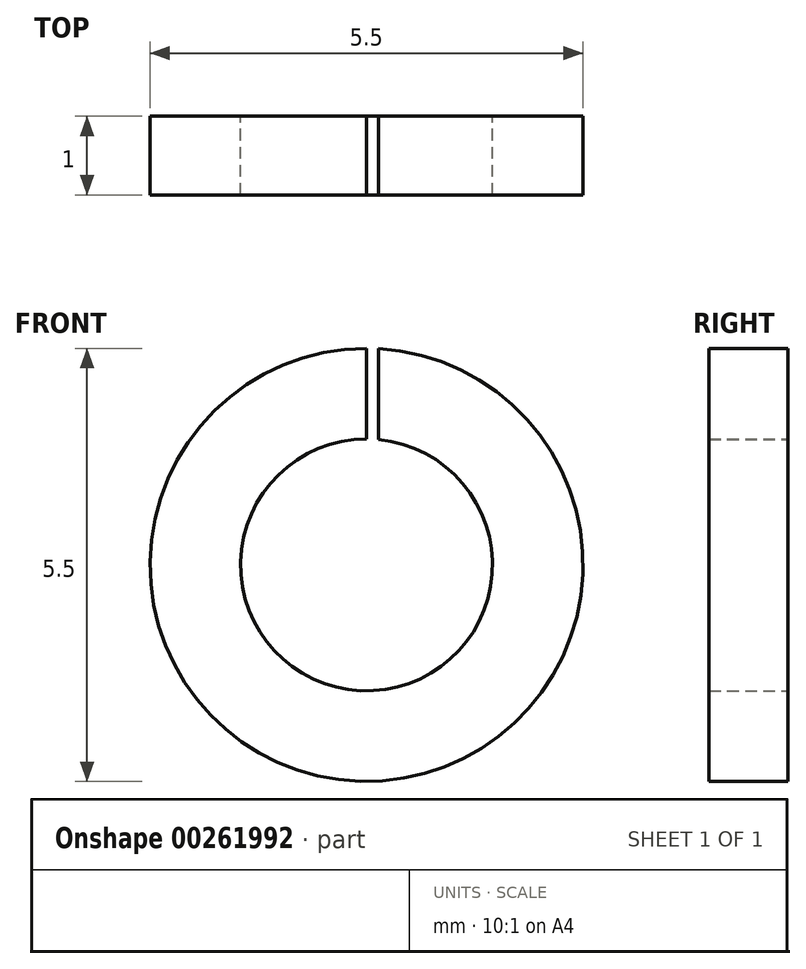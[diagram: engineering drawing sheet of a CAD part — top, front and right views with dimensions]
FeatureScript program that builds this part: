
annotation { "Feature Type Name" : "Feature", "Feature Type Description" : "" }
export const myFeature = defineFeature(function(context is Context, id is Id, definition is map)
    precondition{}
    {
        {
            assignVariable(context, id + "F0", {"name" : "Hieght", "anyValue" : 1});
        }
        {
            var Q0;
            Q0=qCreatedBy(makeId("Front.planeOp"),FACE);
            var sketch = newSketch(context, id + "F1", { "sketchPlane" : qUnion([Q0])});
            skCircle(sketch, "E0", {"center": v(0, 0) * mm, "radius": 1.6 * mm});
            skCircle(sketch, "E1", {"center": v(0, 0) * mm, "radius": 2.75 * mm});
            skSolve(sketch);
        }
        {
            var Q0;
            Q0=makeQuery(id+"F1.imprint","IMPRINT",FACE,{"disambiguationData":[TD([[makeQuery(id+"F1.imprint","IMPRINT",EDGE,{"derivedFrom":sQuery(id+"F1.wireOp",EDGE,"E0")}),-1.0]])]});
            extrude(context, id + "F2", {"entities" : qUnion([Q0]), "depth" : getVariable(context, 'Hieght') * mm});
        }
        {
            var Q0;
            Q0=qCreatedBy(makeId("Front.planeOp"),FACE);
            var sketch = newSketch(context, id + "F3", { "sketchPlane" : qUnion([Q0])});
            skLineSegment(sketch, "E2.bottom", {"start": v(0, 2.75) * mm, "end": v(0.15, 2.75) * mm});
            skLineSegment(sketch, "E2.top", {"start": v(0, 0) * mm, "end": v(0.15, 0) * mm});
            skLineSegment(sketch, "E2.left", {"start": v(0, 2.75) * mm, "end": v(0, 0) * mm});
            skLineSegment(sketch, "E2.right", {"start": v(0.15, 2.75) * mm, "end": v(0.15, 0) * mm});
            skSolve(sketch);
        }
        {
            var Q0;
            Q0=makeQuery(id+"F3.imprint","IMPRINT",FACE,{"disambiguationData":[TD([[makeQuery(id+"F3.imprint","IMPRINT",EDGE,{"derivedFrom":sQuery(id+"F3.wireOp",EDGE,"E2.bottom")}),-1.0]])]});
            extrude(context, id + "F4", {"entities" : qUnion([Q0]), "operationType" : NewBodyOperationType.REMOVE, "depth" : getVariable(context, 'Hieght') * mm});
        }
    });
